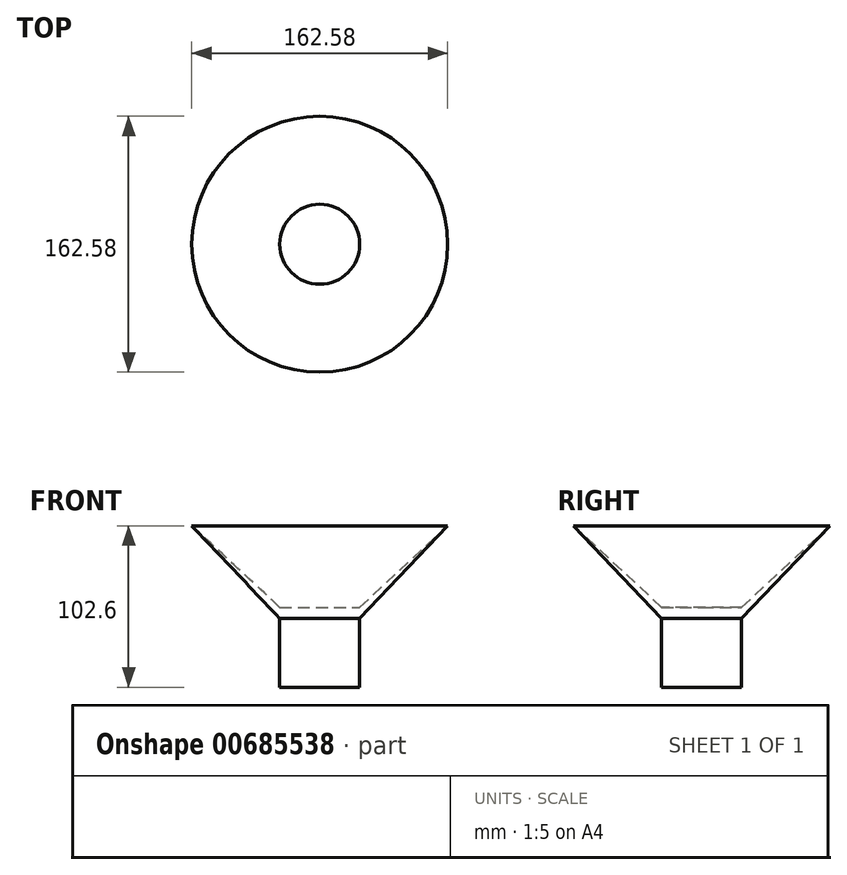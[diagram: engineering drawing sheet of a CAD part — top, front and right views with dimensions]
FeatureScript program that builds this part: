
annotation { "Feature Type Name" : "Feature", "Feature Type Description" : "" }
export const myFeature = defineFeature(function(context is Context, id is Id, definition is map)
    precondition{}
    {
        {
            var Q0;
            Q0=qCreatedBy(makeId("Front.planeOp"),FACE);
            var sketch = newSketch(context, id + "F0", { "sketchPlane" : qUnion([Q0])});
            skLineSegment(sketch, "E0", {"start": v(0, 0) * mm, "end": v(-25.4, 0) * mm});
            skLineSegment(sketch, "E1", {"start": v(-25.4, 0) * mm, "end": v(-25.4, 50.8) * mm});
            skLineSegment(sketch, "E2", {"start": v(-25.4, 50.8) * mm, "end": v(0, 50.8) * mm});
            skLineSegment(sketch, "E3", {"start": v(0, 50.8) * mm, "end": v(55.89, 102.6) * mm});
            skLineSegment(sketch, "E4", {"start": v(55.89, 102.6) * mm, "end": v(0, 43.7) * mm});
            skLineSegment(sketch, "E5", {"start": v(0, 43.7) * mm, "end": v(0, 0) * mm});
            skSolve(sketch);
        }
        {
            var Q0;
            Q0=makeQuery(id+"F0.imprint","IMPRINT",FACE,{"disambiguationData":[TD([[makeQuery(id+"F0.imprint","IMPRINT",EDGE,{"derivedFrom":sQuery(id+"F0.wireOp",EDGE,"E0")}),-1.0]])]});
            var Q1;
            Q1=sQuery(id+"F0.wireOp",EDGE,"E1");
            revolve(context, id + "F1", {"entities" : qUnion([Q0]), "axis" : qUnion([Q1]), "revolveType" : RevolveType.FULL});
        }
    });
